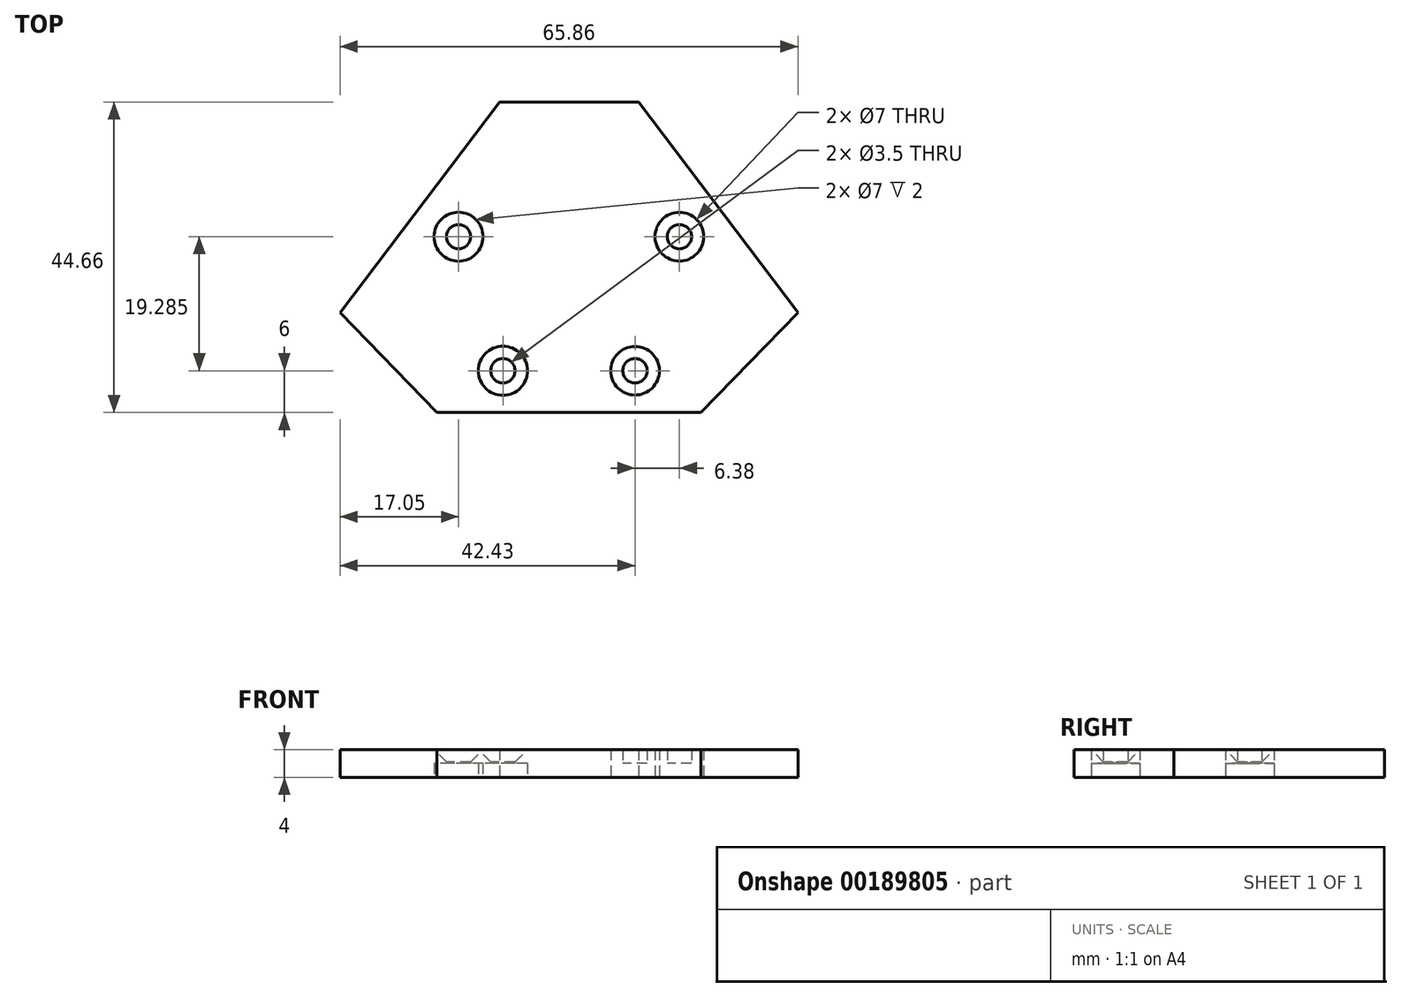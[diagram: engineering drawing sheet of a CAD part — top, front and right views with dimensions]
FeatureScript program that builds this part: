
annotation { "Feature Type Name" : "Feature", "Feature Type Description" : "" }
export const myFeature = defineFeature(function(context is Context, id is Id, definition is map)
    precondition{}
    {
        {
            var Q0;
            Q0=qCreatedBy(makeId("Top.planeOp"),FACE);
            var sketch = newSketch(context, id + "F0", { "sketchPlane" : qUnion([Q0])});
            skLineSegment(sketch, "E0", {"start": v(0, 0) * mm, "end": v(-19, 0) * mm});
            skLineSegment(sketch, "E1", {"start": v(-19, 0) * mm, "end": v(-32.93, 14.36) * mm});
            skLineSegment(sketch, "E2", {"start": v(0, 0) * mm, "end": v(0, 44.66) * mm});
            skLineSegment(sketch, "E3", {"start": v(0, 44.66) * mm, "end": v(-10, 44.66) * mm});
            skLineSegment(sketch, "E4", {"start": v(-10, 44.66) * mm, "end": v(-32.93, 14.36) * mm});
            skLineSegment(sketch, "E5.MirrorCS", {"start": v(0, 0) * mm, "end": v(19, 0) * mm});
            skLineSegment(sketch, "E6.MirrorCS", {"start": v(19, 0) * mm, "end": v(32.93, 14.36) * mm});
            skLineSegment(sketch, "E7.MirrorCS", {"start": v(0, 44.66) * mm, "end": v(10, 44.66) * mm});
            skLineSegment(sketch, "E8.MirrorCS", {"start": v(10, 44.66) * mm, "end": v(32.93, 14.36) * mm});
            skLineSegment(sketch, "E9", {"start": v(-19, 0) * mm, "end": v(-9.5, 0) * mm});
            skCircle(sketch, "E10", {"center": v(-9.5, 6) * mm, "radius": 3.5 * mm});
            skCircle(sketch, "E11", {"center": v(-9.5, 6) * mm, "radius": 1.75 * mm});
            skCircle(sketch, "E12.MirrorC", {"center": v(9.5, 6) * mm, "radius": 1.75 * mm});
            skCircle(sketch, "E13.MirrorC", {"center": v(9.5, 6) * mm, "radius": 3.5 * mm});
            skPoint(sketch, "E14", {"position": v(-15.88, 25.28) * mm});
            skCircle(sketch, "E15", {"center": v(-15.88, 25.28) * mm, "radius": 3.5 * mm});
            skCircle(sketch, "E16", {"center": v(-15.88, 25.28) * mm, "radius": 1.75 * mm});
            skCircle(sketch, "E17.MirrorC", {"center": v(15.88, 25.28) * mm, "radius": 1.75 * mm});
            skCircle(sketch, "E18.MirrorC", {"center": v(15.88, 25.28) * mm, "radius": 3.5 * mm});
            skSolve(sketch);
        }
        {
            var Q0;
            Q0=makeQuery(id+"F0.imprint","IMPRINT",FACE,{"disambiguationData":[TD([[makeQuery(id+"F0.imprint","IMPRINT",EDGE,{"derivedFrom":sQuery(id+"F0.wireOp",EDGE,"E2")}),-1.0]])]});
            var Q1;
            Q1=makeQuery(id+"F0.imprint","IMPRINT",FACE,{"disambiguationData":[TD([[makeQuery(id+"F0.imprint","IMPRINT",EDGE,{"derivedFrom":sQuery(id+"F0.wireOp",EDGE,"E0")}),-1.0]])]});
            extrude(context, id + "F1", {"entities" : qUnion([Q0, Q1]), "depth" : 4 * mm});
        }
        {
            var Q0;
            Q0=makeQuery(id+"F0.imprint","IMPRINT",FACE,{"disambiguationData":[TD([[makeQuery(id+"F0.imprint","IMPRINT",EDGE,{"derivedFrom":sQuery(id+"F0.wireOp",EDGE,"3bpybDuj-MZcf-nzSA-y5HP-1Ucw2PFUD1lN")}),1.0]])]});
            var Q1;
            Q1=makeQuery(id+"F0.imprint","IMPRINT",FACE,{"disambiguationData":[TD([[makeQuery(id+"F0.imprint","IMPRINT",EDGE,{"derivedFrom":sQuery(id+"F0.wireOp",EDGE,"7a818348-4feb-4938-b127-ce05c0f473900.MirrorC")}),-1.0]])]});
            var Q2;
            Q2=makeQuery(id+"F0.imprint","IMPRINT",FACE,{"disambiguationData":[TD([[makeQuery(id+"F0.imprint","IMPRINT",EDGE,{"derivedFrom":sQuery(id+"F0.wireOp",EDGE,"E12.MirrorC")}),1.0]])]});
            var Q3;
            Q3=makeQuery(id+"F0.imprint","IMPRINT",FACE,{"disambiguationData":[TD([[makeQuery(id+"F0.imprint","IMPRINT",EDGE,{"derivedFrom":sQuery(id+"F0.wireOp",EDGE,"E10")}),1.0]])]});
            var Q4;
            Q4=makeQuery(id+"F0.imprint","IMPRINT",FACE,{"disambiguationData":[TD([[makeQuery(id+"F0.imprint","IMPRINT",EDGE,{"derivedFrom":sQuery(id+"F0.wireOp",EDGE,"E15")}),1.0]])]});
            var Q5;
            Q5=makeQuery(id+"F0.imprint","IMPRINT",FACE,{"disambiguationData":[TD([[makeQuery(id+"F0.imprint","IMPRINT",EDGE,{"derivedFrom":sQuery(id+"F0.wireOp",EDGE,"E17.MirrorC")}),1.0]])]});
            extrude(context, id + "F2", {"entities" : qUnion([Q0, Q1, Q2, Q3, Q4, Q5]), "operationType" : NewBodyOperationType.ADD, "depth" : 4 * mm});
        }
        {
            var Q0;
            Q0=makeQuery(id+"F2.opExtrude","CAP_EDGE",EDGE,{"disambiguationData":[OSD([sQuery(id+"F0.wireOp",EDGE,"E17.MirrorC")])],"isStart":false});
            var Q1;
            Q1=makeQuery(id+"F2.opExtrude","CAP_EDGE",EDGE,{"disambiguationData":[OSD([sQuery(id+"F0.wireOp",EDGE,"E16")])],"isStart":false});
            var Q2;
            Q2=makeQuery(id+"F2.opExtrude","CAP_EDGE",EDGE,{"disambiguationData":[OSD([sQuery(id+"F0.wireOp",EDGE,"E11")])],"isStart":false});
            var Q3;
            Q3=makeQuery(id+"F2.opExtrude","CAP_EDGE",EDGE,{"disambiguationData":[OSD([sQuery(id+"F0.wireOp",EDGE,"E12.MirrorC")])],"isStart":false});
            chamfer(context, id + "F3", {"entities" : qUnion([Q0, Q1, Q2, Q3]), "width" : 1.78 * mm, "tangentPropagation" : true});
        }
        {
            var Q0;
            Q0=makeQuery(id+"F0.imprint","IMPRINT",FACE,{"disambiguationData":[TD([[makeQuery(id+"F0.imprint","IMPRINT",EDGE,{"derivedFrom":sQuery(id+"F0.wireOp",EDGE,"E15")}),1.0]])]});
            var Q1;
            Q1=makeQuery(id+"F0.imprint","IMPRINT",FACE,{"disambiguationData":[TD([[makeQuery(id+"F0.imprint","IMPRINT",EDGE,{"derivedFrom":sQuery(id+"F0.wireOp",EDGE,"E17.MirrorC")}),1.0]])]});
            var Q2;
            Q2=makeQuery(id+"F0.imprint","IMPRINT",FACE,{"disambiguationData":[TD([[makeQuery(id+"F0.imprint","IMPRINT",EDGE,{"derivedFrom":sQuery(id+"F0.wireOp",EDGE,"E12.MirrorC")}),1.0]])]});
            var Q3;
            Q3=makeQuery(id+"F0.imprint","IMPRINT",FACE,{"disambiguationData":[TD([[makeQuery(id+"F0.imprint","IMPRINT",EDGE,{"derivedFrom":sQuery(id+"F0.wireOp",EDGE,"E10")}),1.0]])]});
            extrude(context, id + "F4", {"entities" : qUnion([Q0, Q1, Q2, Q3]), "operationType" : NewBodyOperationType.REMOVE, "offsetDistance" : 25 * mm, "depth" : 2 * mm});
        }
    });
